# Revit family: QF_BOURGEAT_3GN_et4GN_vitrine_refrigeree_3nv
name_source: partatom
category: Equipement spécialisé
revit_build: Autodesk Revit 2015 (Build: 20140606_1530(x64)
units: mm (PartAtom-declared; Revit-internal decimal feet)

## types (36) — shared parameters
Certification = NF alimentaire
Charge max = 200.00 kg
Classe Climatique = 3
Fabricant = BOURGEAT
Fréquence = 50 Hz
Hauteur hors tout = 1800 mm  [stored 5.90551 ft]
Indice de protection = 21
Intensité nominale = 10 A
Nature isolant = polyurethane
Niveau Sonore = 60dBa
Phase = 2
Profondeur hors tout = 820 mm  [stored 2.69029 ft]
Spécification du Fabricant = vitrine réfrigérée 3 niveaux OASIS
Tension = 230 V
Type Fluide Frigorigène = R404a
URL catalogue = http://www.bourgeat.fr
lg_porte_groupe_froid = 569 mm  [stored 1.8668 ft]

## per-type parameters (varying)
| type | Etageres | Longueur hors tout | Modèle | Pieds | Poids net à vide | Puissance frigorifique | Puissance électrique  | Roues | cuve_plate | lg_etageres | lg_vitrine | profondeur_cuve | reserve |
| 4GN_baie_libre_cuve_plate_roues | Non | 1660 mm  [stored 5.44619 ft] | 853104 + 854950 | Non | 335.00 kg | 1185W | 2300 W | Oui | Oui | 736 mm  [stored 2.4147 ft] | 1525 mm  [stored 5.00328 ft] | 0 mm  [stored 0 ft] | Non |
| 4GN_baie_libre_cuve90 | Non | 1660 mm  [stored 5.44619 ft] | 853194 | Oui | 335.00 kg | 1185W | 2300 W | Non | Non | 736 mm  [stored 2.4147 ft] | 1525 mm  [stored 5.00328 ft] | 90 mm  [stored 0.295276 ft] | Non |
| 4GN_reserve_cuve90 | Non | 1660 mm  [stored 5.44619 ft] | 853494 | Oui | 335.00 kg | 1440W | 2300 W | Non | Non | 736 mm  [stored 2.4147 ft] | 1525 mm  [stored 5.00328 ft] | 90 mm  [stored 0.295276 ft] | Oui |
| 4GN_reserve_cuve_plate | Non | 1660 mm  [stored 5.44619 ft] | 853404 | Oui | 335.00 kg | 1440W | 2300 W | Non | Oui | 736 mm  [stored 2.4147 ft] | 1525 mm  [stored 5.00328 ft] | 0 mm  [stored 0 ft] | Oui |
| 4GN_baie_libre_cuve90_roues | Non | 1660 mm  [stored 5.44619 ft] | 853194 + 854950 | Non | 335.00 kg | 1185W | 2300 W | Oui | Non | 736 mm  [stored 2.4147 ft] | 1525 mm  [stored 5.00328 ft] | 90 mm  [stored 0.295276 ft] | Non |
| 4GN_reserve_cuve_plate_roues | Non | 1660 mm  [stored 5.44619 ft] | 853404 + 854950 | Oui | 335.00 kg | 1440W | 2300 W | Non | Oui | 736 mm  [stored 2.4147 ft] | 1525 mm  [stored 5.00328 ft] | 0 mm  [stored 0 ft] | Oui |
| 4GN_reserve_cuve90_roues | Non | 1660 mm  [stored 5.44619 ft] | 853494 + 854950 | Non | 335.00 kg | 1440W | 2300 W | Oui | Non | 736 mm  [stored 2.4147 ft] | 1525 mm  [stored 5.00328 ft] | 90 mm  [stored 0.295276 ft] | Oui |
| 4GN_baie_libre_cuve_plate | Non | 1660 mm  [stored 5.44619 ft] | 853104 | Oui | 355.00 kg | 1185W | 2300 W | Non | Oui | 736 mm  [stored 2.4147 ft] | 1525 mm  [stored 5.00328 ft] | 0 mm  [stored 0 ft] | Non |
| 4GN_baie_libre_cuve_plate_etageres | Oui | 1660 mm  [stored 5.44619 ft] | 853104 + 854924 | Oui | 335.00 kg | 1185W | 2300 W | Non | Oui | 736 mm  [stored 2.4147 ft] | 1525 mm  [stored 5.00328 ft] | 0 mm  [stored 0 ft] | Non |
| 4GN_baie_libre_cuve90_etageres | Oui | 1660 mm  [stored 5.44619 ft] | 853194 + 859424 | Oui | 335.00 kg | 1185W | 2300 W | Non | Non | 736 mm  [stored 2.4147 ft] | 1525 mm  [stored 5.00328 ft] | 90 mm  [stored 0.295276 ft] | Non |
| 4GN_baie_libre_cuve90_etageres_roues | Oui | 1660 mm  [stored 5.44619 ft] | 853194 + 859424 + 854950 | Non | 335.00 kg | 1185W | 2300 W | Oui | Non | 736 mm  [stored 2.4147 ft] | 1525 mm  [stored 5.00328 ft] | 90 mm  [stored 0.295276 ft] | Non |
| 4GN_baie_libre_cuve_plate_etageres_roues | Oui | 1660 mm  [stored 5.44619 ft] | 853104 + 854924 + 854950 | Non | 335.00 kg | 1185W | 2300 W | Oui | Oui | 736 mm  [stored 2.4147 ft] | 1525 mm  [stored 5.00328 ft] | 0 mm  [stored 0 ft] | Non |
| 3GN_baie_libre_cuve_plate | Non | 1465 mm  [stored 4.80643 ft] | 853133 | Oui | 315.00 kg | 1185W | 2200 W | Non | Oui | 541 mm | 1330 mm  [stored 4.36352 ft] | 0 mm  [stored 0 ft] | Non |
| 3GN_baie_libre_cuve90 | Non | 1465 mm  [stored 4.80643 ft] | 853193 | Oui | 315.00 kg | 1185W | 2200 W | Non | Non | 541 mm | 1330 mm  [stored 4.36352 ft] | 90 mm  [stored 0.295276 ft] | Non |
| 3GN_baie_libre_cuve_plate_roues | Non | 1465 mm  [stored 4.80643 ft] | 853133 + 854950 | Non | 315.00 kg | 1185W | 2200 W | Oui | Oui | 541 mm | 1330 mm  [stored 4.36352 ft] | 0 mm  [stored 0 ft] | Non |
| 3GN_baie_libre_cuve90_roues | Non | 1465 mm  [stored 4.80643 ft] | 853193 + 854950 | Non | 315.00 kg | 1440W | 2200 W | Oui | Non | 541 mm | 1330 mm  [stored 4.36352 ft] | 90 mm  [stored 0.295276 ft] | Non |
| 3GN_reserve_cuve90 | Non | 1465 mm  [stored 4.80643 ft] | 853493 | Oui | 315.00 kg | 1440W | 2300 W | Non | Non | 541 mm | 1330 mm  [stored 4.36352 ft] | 90 mm  [stored 0.295276 ft] | Oui |
| 3GN_reserve_cuve_plate | Non | 1465 mm  [stored 4.80643 ft] | 853403 | Oui | 315.00 kg | 1440W | 2200 W | Non | Oui | 541 mm | 1330 mm  [stored 4.36352 ft] | 0 mm  [stored 0 ft] | Oui |
| 3GN_reserve_cuve_plate_roues | Non | 1465 mm  [stored 4.80643 ft] | 853403 + 854950 | Non | 315.00 kg | 1440W | 2300 W | Oui | Oui | 541 mm | 1330 mm  [stored 4.36352 ft] | 0 mm  [stored 0 ft] | Oui |
| 3GN_reserve_cuve90_roues | Non | 1465 mm  [stored 4.80643 ft] | 853493 | Non | 315.00 kg | 1440W | 2300 W | Oui | Non | 541 mm | 1330 mm  [stored 4.36352 ft] | 90 mm  [stored 0.295276 ft] | Oui |
| 3GN_baie_libre_cuve_plate_etageres | Oui | 1465 mm  [stored 4.80643 ft] | 853133 + 854923 | Oui | 315.00 kg | 1185W | 2200 W | Non | Oui | 541 mm | 1330 mm  [stored 4.36352 ft] | 0 mm  [stored 0 ft] | Non |
| 3GN_baie_libre_cuve90_etageres | Oui | 1465 mm  [stored 4.80643 ft] | 853193 + 854923 | Oui | 315.00 kg | 1185W | 2200 W | Non | Non | 541 mm | 1330 mm  [stored 4.36352 ft] | 90 mm  [stored 0.295276 ft] | Non |
| 3GN_baie_libre_cuve90_etageres_roues | Oui | 1465 mm  [stored 4.80643 ft] | 853193 + 854923 + 854950 | Non | 315.00 kg | 1185W | 2200 W | Oui | Non | 541 mm | 1330 mm  [stored 4.36352 ft] | 90 mm  [stored 0.295276 ft] | Non |
| 3GN_baie_libre_cuve_plate_etageres_roues | Oui | 1465 mm  [stored 4.80643 ft] | 853133 + 854923 + 854950 | Non | 315.00 kg | 1185W | 2200 W | Oui | Oui | 541 mm | 1330 mm  [stored 4.36352 ft] | 0 mm  [stored 0 ft] | Non |
| 3GN_baie_libre_cuve_30 | Non | 1465 mm  [stored 4.80643 ft] | 853233 | Oui | 315.00 kg | 1185W | 2200 W | Non | Oui | 541 mm | 1330 mm  [stored 4.36352 ft] | 30 mm  [stored 0.0984252 ft] | Non |
| 3GN_baie_libre_cuve_30_etageres | Oui | 1465 mm  [stored 4.80643 ft] | 853233 + 854923 | Oui | 315.00 kg | 1185W | 2200 W | Non | Oui | 541 mm | 1330 mm  [stored 4.36352 ft] | 30 mm  [stored 0.0984252 ft] | Non |
| 3GN_baie_libre_cuve_30_etageres_roues | Oui | 1465 mm  [stored 4.80643 ft] | 853233 + 854923 + 854950 | Non | 315.00 kg | 1185W | 2200 W | Oui | Oui | 541 mm | 1330 mm  [stored 4.36352 ft] | 30 mm  [stored 0.0984252 ft] | Non |
| 3GN_baie_libre_cuve_30_roues | Non | 1465 mm  [stored 4.80643 ft] | 853233 + 854950 | Non | 315.00 kg | 1185W | 2200 W | Oui | Oui | 541 mm | 1330 mm  [stored 4.36352 ft] | 30 mm  [stored 0.0984252 ft] | Non |
| 3GN_reserve_cuve_30 | Non | 1465 mm  [stored 4.80643 ft] | 853603 | Oui | 315.00 kg | 1440W | 2200 W | Non | Oui | 541 mm | 1330 mm  [stored 4.36352 ft] | 30 mm  [stored 0.0984252 ft] | Oui |
| 3GN_reserve_cuve_30_roues | Non | 1465 mm  [stored 4.80643 ft] | 853603 + 854950 | Non | 315.00 kg | 1440W | 2300 W | Oui | Oui | 541 mm | 1330 mm  [stored 4.36352 ft] | 30 mm  [stored 0.0984252 ft] | Oui |
| 4GN_baie_libre_cuve_30 | Non | 1660 mm  [stored 5.44619 ft] | 853204 | Oui | 355.00 kg | 1185W | 2300 W | Non | Oui | 736 mm  [stored 2.4147 ft] | 1525 mm  [stored 5.00328 ft] | 30 mm  [stored 0.0984252 ft] | Non |
| 4GN_baie_libre_cuve_30_etageres | Oui | 1660 mm  [stored 5.44619 ft] | 853204 + 854924 | Oui | 335.00 kg | 1185W | 2300 W | Non | Oui | 736 mm  [stored 2.4147 ft] | 1525 mm  [stored 5.00328 ft] | 30 mm  [stored 0.0984252 ft] | Non |
| 4GN_baie_libre_cuve_30_etageres_roues | Oui | 1660 mm  [stored 5.44619 ft] | 853204 + 854924 + 854950 | Non | 335.00 kg | 1185W | 2300 W | Oui | Oui | 736 mm  [stored 2.4147 ft] | 1525 mm  [stored 5.00328 ft] | 30 mm  [stored 0.0984252 ft] | Non |
| 4GN_baie_libre_cuve_30_roues | Non | 1660 mm  [stored 5.44619 ft] | 853204 + 854950 | Non | 335.00 kg | 1185W | 2300 W | Oui | Oui | 736 mm  [stored 2.4147 ft] | 1525 mm  [stored 5.00328 ft] | 30 mm  [stored 0.0984252 ft] | Non |
| 4GN_reserve_cuve_30 | Non | 1660 mm  [stored 5.44619 ft] | 853604 | Oui | 335.00 kg | 1440W | 2300 W | Non | Oui | 736 mm  [stored 2.4147 ft] | 1525 mm  [stored 5.00328 ft] | 30 mm  [stored 0.0984252 ft] | Oui |
| 4GN_reserve_cuve_30_roues | Non | 1660 mm  [stored 5.44619 ft] | 853604 + 854950 | Oui | 335.00 kg | 1440W | 2300 W | Non | Oui | 736 mm  [stored 2.4147 ft] | 1525 mm  [stored 5.00328 ft] | 30 mm  [stored 0.0984252 ft] | Oui |

note: [stored X ft] marks values corroborated as IEEE doubles in the binary element streams (Revit-internal decimal feet)

## geometry (parser evidence)
native form markers: Blend x6
no freeform markers — native parametric forms only
